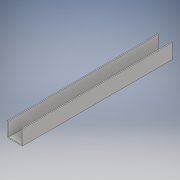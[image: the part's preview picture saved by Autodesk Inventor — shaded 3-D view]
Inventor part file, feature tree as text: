
AUTODESK INVENTOR PART (.ipt)
format: ipt  version: 2017 (Build 210142000, 142)  size: 98,816 bytes
history: native  units: in
note: dims shown in document units (in); Inventor stores cm internally (conversion verified against a paired STEP export)
features: sketch x2, extrude x1
ambient origin geometry x8: Origin, YZ Plane, XZ Plane, XY Plane, X Axis, Y Axis, Z Axis, Center Point
bodies: Solid1 (feature_tree)
feature tree (3):
  sketch  "Sketch1"  dims[d2=0.079in d3=1.26in]
  sketch  "Sketch2"  dims[d5=12.75in d6=0.0in]
  extrude  "Extrusion1"  Depth=1.26in
